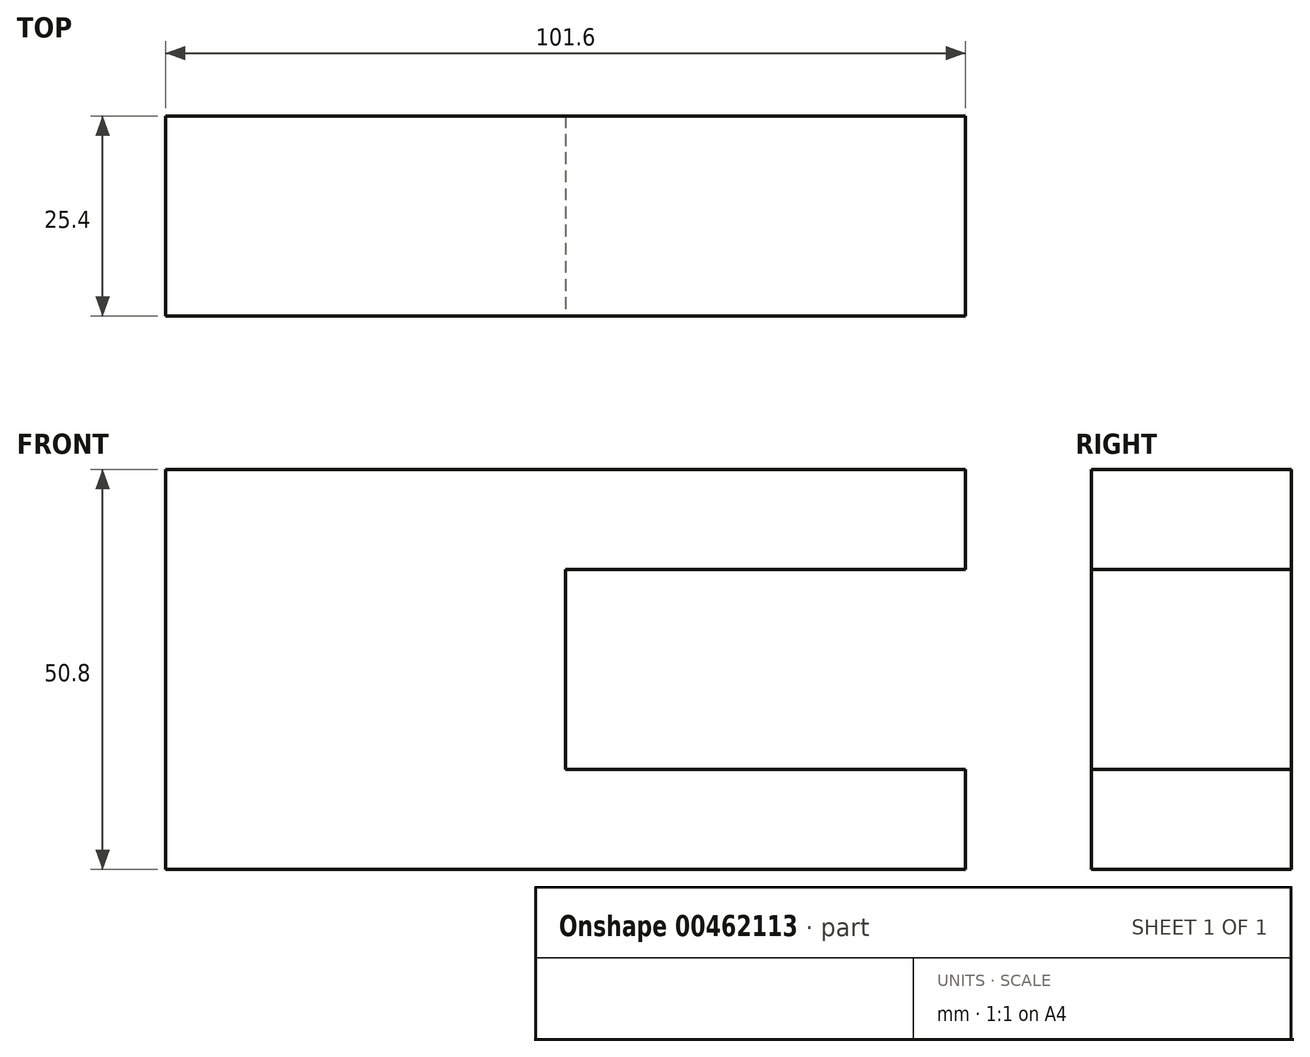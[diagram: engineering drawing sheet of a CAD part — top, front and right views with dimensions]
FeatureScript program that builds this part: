
annotation { "Feature Type Name" : "Feature", "Feature Type Description" : "" }
export const myFeature = defineFeature(function(context is Context, id is Id, definition is map)
    precondition{}
    {
        {
            var Q0;
            Q0=qCreatedBy(makeId("Front.planeOp"),FACE);
            var sketch = newSketch(context, id + "F0", { "sketchPlane" : qUnion([Q0])});
            skLineSegment(sketch, "E0.bottom", {"start": v(50.8, 25.4) * mm, "end": v(-50.8, 25.4) * mm});
            skLineSegment(sketch, "E0.top", {"start": v(50.8, -25.4) * mm, "end": v(-50.8, -25.4) * mm});
            skLineSegment(sketch, "E0.left", {"start": v(50.8, 25.4) * mm, "end": v(50.8, -25.4) * mm});
            skLineSegment(sketch, "E0.right", {"start": v(-50.8, 25.4) * mm, "end": v(-50.8, -25.4) * mm});
            skPoint(sketch, "E0.middle", {"position": v(0, 0) * mm});
            skSolve(sketch);
        }
        {
            var Q0;
            Q0=qSketchRegion(id+"F0",true);
            extrude(context, id + "F1", {"entities" : qUnion([Q0]), "depth" : 25.4 * mm});
        }
        {
            var Q0;
            Q0=makeQuery(id+"F1.opExtrude","CAP_FACE",FACE,{"disambiguationData":[OSD([sQuery(id+"F0.wireOp",EDGE,"E0.bottom"),sQuery(id+"F0.wireOp",EDGE,"E0.top"),sQuery(id+"F0.wireOp",EDGE,"E0.left"),sQuery(id+"F0.wireOp",EDGE,"E0.right")])],"isStart":false});
            var sketch = newSketch(context, id + "F2", { "sketchPlane" : qUnion([Q0])});
            skLineSegment(sketch, "E1.bottom", {"start": v(50.8, 12.7) * mm, "end": v(0, 12.7) * mm});
            skLineSegment(sketch, "E1.top", {"start": v(50.8, -12.7) * mm, "end": v(0, -12.7) * mm});
            skLineSegment(sketch, "E1.left", {"start": v(50.8, 12.7) * mm, "end": v(50.8, -12.7) * mm});
            skLineSegment(sketch, "E1.right", {"start": v(0, 12.7) * mm, "end": v(0, -12.7) * mm});
            skSolve(sketch);
        }
        {
            var Q0;
            Q0=qSketchRegion(id+"F2",true);
            extrude(context, id + "F3", {"entities" : qUnion([Q0]), "operationType" : NewBodyOperationType.REMOVE, "endBound" : BoundingType.THROUGH_ALL, "oppositeDirection" : true, "depth" : 25.4 * mm});
        }
    });
